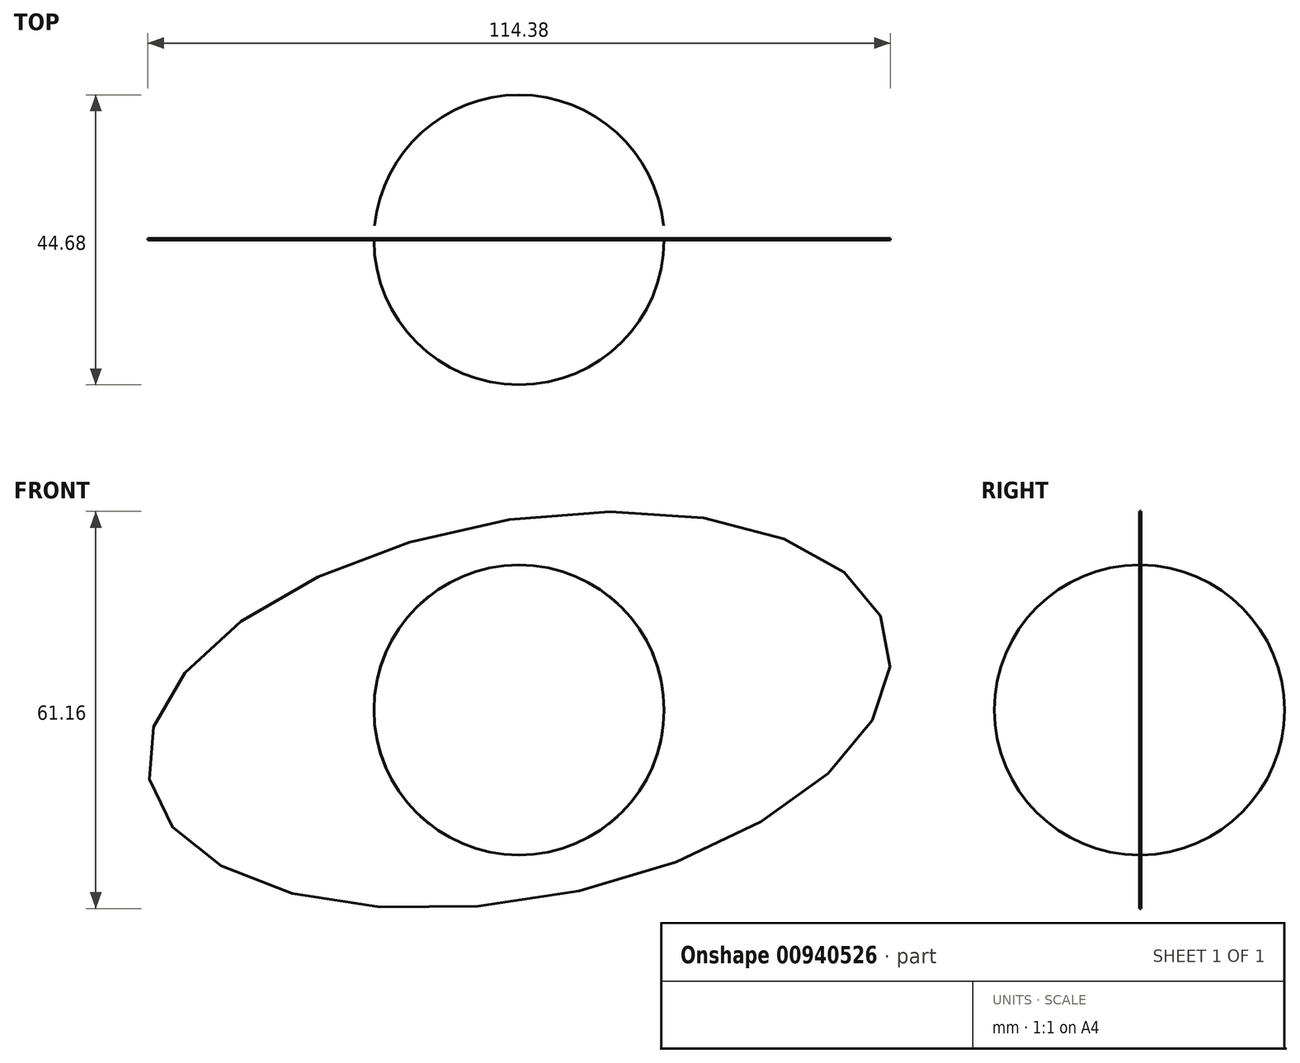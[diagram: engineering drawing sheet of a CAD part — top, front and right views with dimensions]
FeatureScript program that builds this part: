
annotation { "Feature Type Name" : "Feature", "Feature Type Description" : "" }
export const myFeature = defineFeature(function(context is Context, id is Id, definition is map)
    precondition{}
    {
        {
            var Q0;
            Q0=qCreatedBy(makeId("Top.planeOp"),FACE);
            var sketch = newSketch(context, id + "F0", { "sketchPlane" : qUnion([Q0])});
            skArc(sketch, "E0", {"start": v(-22.34, 0) * mm, "mid": v(0, -22.34) * mm, "end": v(22.34, 0) * mm});
            skLineSegment(sketch, "E1", {"start": v(-22.34, 0) * mm, "end": v(22.34, 0) * mm});
            skSolve(sketch);
        }
        {
            var Q0;
            Q0 = qSketchRegion(id + "F0", true);
            var Q1;
            Q1=sQuery(id+"F0.wireOp",EDGE,"E1");
            revolve(context, id + "F1", {"surfaceOperationType" : NewSurfaceOperationType.NEW, "entities" : qUnion([Q0]), "axis" : qUnion([Q1]), "revolveType" : RevolveType.FULL});
        }
        {
            var Q0;
            Q0=qCreatedBy(makeId("Front.planeOp"),FACE);
            var sketch = newSketch(context, id + "F2", { "sketchPlane" : qUnion([Q0])});
            skEllipse(sketch, "E2", {"center": v(0, 0) * mm, "majorRadius": 57.94 * mm, "minorRadius": 29.15 * mm, "majorAxis": v(-0.98, -0.18)});
            skSolve(sketch);
        }
        {
            var Q0;
            Q0 = qSketchRegion(id + "F2", true);
            extrude(context, id + "F3", {"entities" : qUnion([Q0]), "operationType" : NewBodyOperationType.ADD, "oppositeDirection" : true, "depth" : 0.25 * mm, "offsetDistance" : 25.4 * mm});
        }
    });
